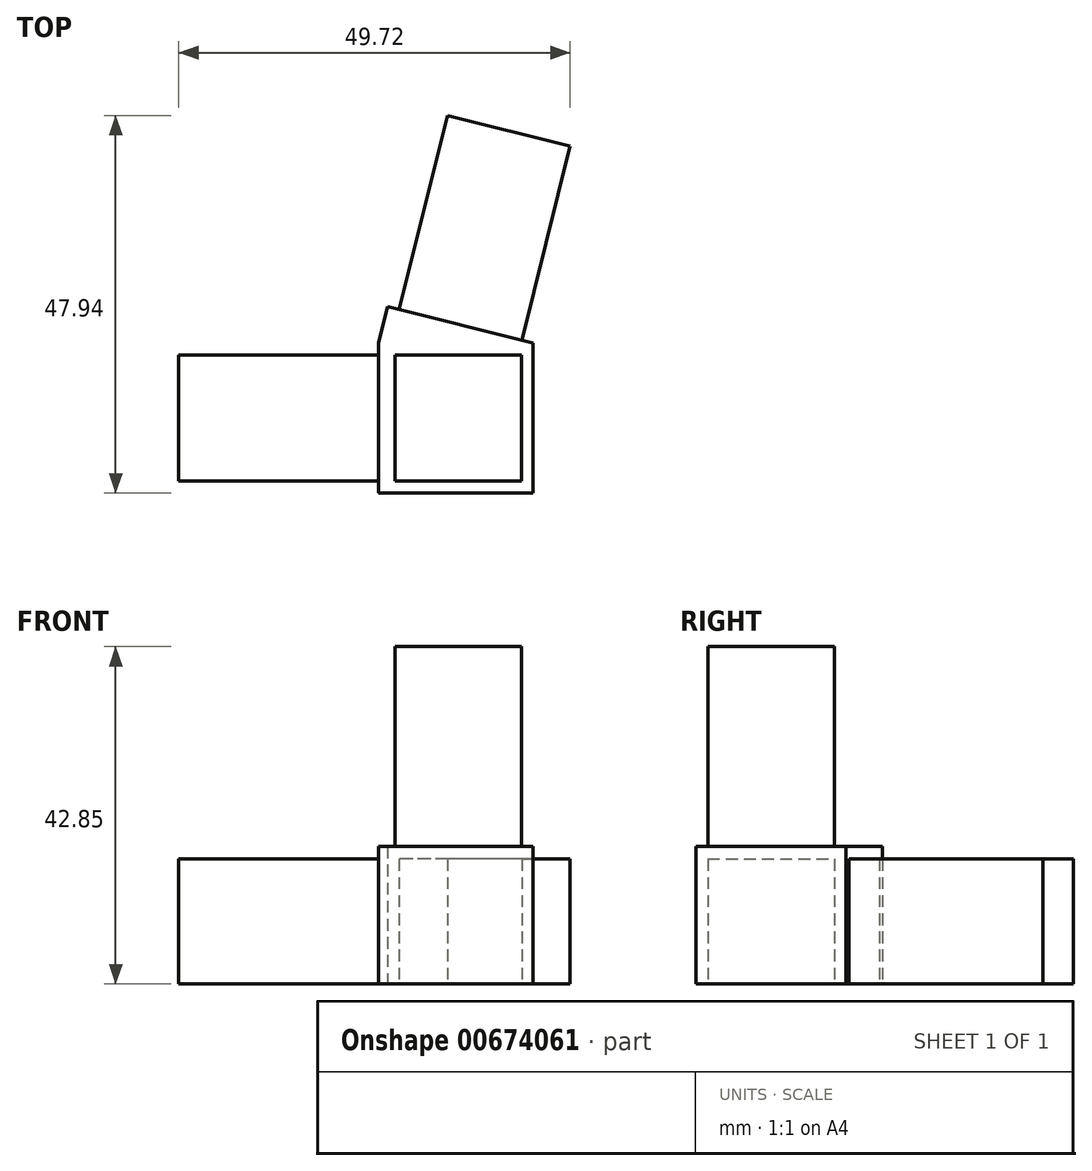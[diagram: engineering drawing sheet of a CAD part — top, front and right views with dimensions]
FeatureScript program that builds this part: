
annotation { "Feature Type Name" : "Feature", "Feature Type Description" : "" }
export const myFeature = defineFeature(function(context is Context, id is Id, definition is map)
    precondition{}
    {
        {
            var Q0;
            Q0=qCreatedBy(makeId("Top.planeOp"),FACE);
            var sketch = newSketch(context, id + "F0", { "sketchPlane" : qUnion([Q0])});
            skLineSegment(sketch, "E0", {"start": v(0, 0) * mm, "end": v(0, 19.05) * mm});
            skLineSegment(sketch, "E1", {"start": v(0, 19.05) * mm, "end": v(-1.46, 19.41) * mm});
            skLineSegment(sketch, "E2", {"start": v(-1.46, 19.41) * mm, "end": v(4.69, 44.06) * mm});
            skLineSegment(sketch, "E3", {"start": v(4.69, 44.06) * mm, "end": v(-10.88, 47.94) * mm});
            skLineSegment(sketch, "E4", {"start": v(-10.88, 47.94) * mm, "end": v(-17.03, 23.3) * mm});
            skLineSegment(sketch, "E5", {"start": v(-17.03, 23.3) * mm, "end": v(-18.48, 23.66) * mm});
            skLineSegment(sketch, "E6", {"start": v(0, 0) * mm, "end": v(-19.63, 0) * mm});
            skLineSegment(sketch, "E7", {"start": v(-19.63, 0) * mm, "end": v(-19.63, 1.5) * mm});
            skLineSegment(sketch, "E8", {"start": v(-19.63, 1.5) * mm, "end": v(-45.03, 1.5) * mm});
            skLineSegment(sketch, "E9", {"start": v(-45.03, 1.5) * mm, "end": v(-45.03, 17.55) * mm});
            skLineSegment(sketch, "E10", {"start": v(-45.03, 17.55) * mm, "end": v(-19.63, 17.55) * mm});
            skLineSegment(sketch, "E11", {"start": v(-19.63, 17.55) * mm, "end": v(-19.63, 19.05) * mm});
            skLineSegment(sketch, "E12", {"start": v(-18.48, 23.66) * mm, "end": v(-19.63, 19.05) * mm});
            skSolve(sketch);
        }
        {
            var Q0;
            Q0=makeQuery(id+"F0.imprint","IMPRINT",FACE,{"disambiguationData":[TD([[makeQuery(id+"F0.imprint","IMPRINT",EDGE,{"derivedFrom":sQuery(id+"F0.wireOp",EDGE,"E0")}),1.0]])]});
            extrude(context, id + "F1", {"entities" : qUnion([Q0]), "depth" : 15.85 * mm, "offsetDistance" : 25 * mm});
        }
        {
            var Q0;
            Q0=makeQuery(id+"F1.opExtrude","CAP_FACE",FACE,{"disambiguationData":[OSD([sQuery(id+"F0.wireOp",EDGE,"E0"),sQuery(id+"F0.wireOp",EDGE,"E1"),sQuery(id+"F0.wireOp",EDGE,"E2"),sQuery(id+"F0.wireOp",EDGE,"E3"),sQuery(id+"F0.wireOp",EDGE,"E4"),sQuery(id+"F0.wireOp",EDGE,"E5"),sQuery(id+"F0.wireOp",EDGE,"E6"),sQuery(id+"F0.wireOp",EDGE,"E7"),sQuery(id+"F0.wireOp",EDGE,"E8"),sQuery(id+"F0.wireOp",EDGE,"E9"),sQuery(id+"F0.wireOp",EDGE,"E10"),sQuery(id+"F0.wireOp",EDGE,"E11"),sQuery(id+"F0.wireOp",EDGE,"E12")])],"isStart":false});
            var sketch = newSketch(context, id + "F2", { "sketchPlane" : qUnion([Q0])});
            skLineSegment(sketch, "E13", {"start": v(-19.63, 0) * mm, "end": v(-19.63, 19.05) * mm});
            skLineSegment(sketch, "E14", {"start": v(-19.63, 19.05) * mm, "end": v(-18.48, 23.66) * mm});
            skLineSegment(sketch, "E15", {"start": v(-18.48, 23.66) * mm, "end": v(0, 19.05) * mm});
            skLineSegment(sketch, "E16", {"start": v(0, 19.05) * mm, "end": v(0, 0) * mm});
            skLineSegment(sketch, "E17", {"start": v(0, 0) * mm, "end": v(-19.63, 0) * mm});
            skSolve(sketch);
        }
        {
            var Q0;
            {var subQ0=sQuery(id+"F2.wireOp",EDGE,"E14");Q0=makeQuery(id+"F2.imprint","IMPRINT",FACE,{"disambiguationData":[TD([[makeQuery(id+"F2.imprint","IMPRINT",EDGE,{"derivedFrom":subQ0}),1.0]])]});}
            extrude(context, id + "F3", {"entities" : qUnion([Q0]), "operationType" : NewBodyOperationType.ADD, "depth" : 1.6 * mm, "offsetDistance" : 25 * mm});
        }
        {
            var Q0;
            Q0=makeQuery(id+"F3.opExtrude","CAP_FACE",FACE,{"disambiguationData":[OSD([sQuery(id+"F2.wireOp",EDGE,"E13"),sQuery(id+"F2.wireOp",EDGE,"E14"),sQuery(id+"F2.wireOp",EDGE,"E15"),sQuery(id+"F2.wireOp",EDGE,"E16"),sQuery(id+"F2.wireOp",EDGE,"E17")])],"isStart":false});
            var sketch = newSketch(context, id + "F4", { "sketchPlane" : qUnion([Q0])});
            skLineSegment(sketch, "E18", {"start": v(-1.5, 1.5) * mm, "end": v(-17.55, 1.5) * mm});
            skLineSegment(sketch, "E19", {"start": v(-17.55, 1.5) * mm, "end": v(-17.55, 17.55) * mm});
            skLineSegment(sketch, "E20", {"start": v(-17.55, 17.55) * mm, "end": v(-1.5, 17.55) * mm});
            skLineSegment(sketch, "E21", {"start": v(-1.5, 17.55) * mm, "end": v(-1.5, 1.5) * mm});
            skSolve(sketch);
        }
        {
            var Q0;
            Q0=makeQuery(id+"F4.imprint","IMPRINT",FACE,{"disambiguationData":[TD([[makeQuery(id+"F4.imprint","IMPRINT",EDGE,{"derivedFrom":sQuery(id+"F4.wireOp",EDGE,"E18")}),-1.0]])]});
            extrude(context, id + "F5", {"entities" : qUnion([Q0]), "operationType" : NewBodyOperationType.ADD, "depth" : 25.4 * mm, "offsetDistance" : 25 * mm});
        }
    });
